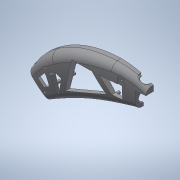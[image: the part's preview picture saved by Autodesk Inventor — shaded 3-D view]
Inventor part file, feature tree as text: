
AUTODESK INVENTOR PART (.ipt)
format: ipt  version: 2020 (Build 240168000, 168)  size: 6,243,840 bytes
history: native  units: in
note: dims shown in document units (in); Inventor stores cm internally (conversion verified against a paired STEP export)
features: extrude x17, sketch x9, other x5, fillet x4, projected_geometry x4, surface_op x2, revolve x2, boolean_combine x1, split x1, chamfer x1, plane x1, delete_face x1, mirror x1, imported_body x1
ambient origin geometry x8: Origin, YZ Plane, XZ Plane, XY Plane, X Axis, Y Axis, Z Axis, Center Point
bodies: Solid1 (feature_tree), Solid196 (feature_tree), Solid197 (feature_tree)
feature tree (50):
  other  "Repaired Geometry1"
  surface_op  "Stitch Surface1"
  sketch  "Sketch2-<F>"  dims[d0=0.03in d1=0.198in]
  extrude  "Extrusion1"  Depth=0.198in
  extrude  "Extrusion2"  Depth=0.184in
  surface_op  "Stitch Surface2"
  boolean_combine  "Combine2"
  split  "Split1"
  extrude  "Extrusion4"  Depth=0.268in
  sketch  "Sketch5-<F>"  dims[d2=0.21in d3=0.184in]
  extrude  "Extrusion5"  Depth=0.4in
  extrude  "Extrusion6"  Depth=0.158in TaperAngle=0.0deg
  extrude  "Extrusion7"  Depth=0.03in
  sketch  "Sketch7-<F>"  dims[d4=0.158in d5=0.0in d7=0.268in]
  extrude  "Extrusion8"  Depth=0.329in
  revolve  "Revolution1"  [1 undecoded]
  revolve  "Revolution2"  [1 undecoded]
  fillet  "Fillet1"  Radius=1.086in
  extrude  "Extrusion9"  Depth=0.423in
  sketch  "Sketch8-<F>"  dims[d8=1.512in d9=0.4in]
  extrude  "Extrusion10"  Depth=0.88in
  extrude  "Extrusion11"  Depth=1.0in
  extrude  "Extrusion12"  Depth=1.03in
  extrude  "Extrusion13"  Depth=1.053in
  chamfer  "Chamfer1"  Distance=1.125in
  extrude  "Extrusion14"  Depth=0.044in
  plane  "Work Plane2"
  extrude  "Extrusion15"  Depth=0.09in
  extrude  "Extrusion16"  Depth=0.17in
  delete_face  "Delete Face2"
  extrude  "Extrusion17"  Depth=0.24in
  fillet  "Fillet3"  Radius=0.244in
  fillet  "Fillet4"  Radius=0.025in
  fillet  "Fillet5"  Radius=0.016in
  mirror  "Mirror1"
  extrude  "Extrusion18"  Depth=0.097in
  other  "Srf3"
  other  "Srf4"
  imported_body  "Base1"
  sketch  "Sketch6-<F>"  dims[d10=0.7in d11=0.158in d12=0.0in]
  sketch  "Sketch9-<F>"  dims[d16=0.004in d17=0.004in d18=0.03in]
  sketch  "Sketch10-<F>"  dims[d19=0.07in]
  projected_geometry  "Projected Loop1"
  sketch  "Sketch11-<F>"  dims[d20=0.031in d45=0.121in d46=0.03in d47=0.158in d48=0.03in d49=0.03in d50=0.03in d51=0.03in d52=0.03in d53=0.03in d54=0.03in d55=0.06in d56=0.03in d57=0.03in d59=0.0962in d60=0.329in]
  sketch  "Sketch12-<F>"  dims[d61=0.595in d62=0.85in d63=0.975in d64=1.086in d66=0.423in d67=0.88in d68=1.0in d69=1.03in d70=1.053in d71=1.125in d72=0.044in d73=0.09in d74=0.17in d75=0.24in d76=0.244in d77=0.025in d78=0.016in d79=0.097in d80=0.23in d83=0.225in d84=0.4in d85=0.4055in d86=0.4785in d87=0.4in d88=0.05in d89=1.2in d90=0.0625in d91=0.0in d92=0.2205in d93=0.0206in d94=0.0495in d95=0.0in d96=0.0755in d97=0.0in d124=0.043in d131=0.055in d132=0.11in d133=0.055in d134=0.0235in d135=0.086in d136=0.043in d139=0.045in d141=0.043in d147=0.0235in d148=0.11in d149=0.055in d150=0.2508in d151=0.075in d153=0.0035in d154=0.0035in d155=0.043in d156=0.045in d157=0.055in d158=0.0in d159=90.0deg d160=90.0deg d161=0.04in d162=0.091in d163=0.034in d164=0.064in d165=0.3105in d166=0.025in d167=0.025in d168=0.025in d169=0.025in d170=1.065in d171=1.0in d172=0.0in d173=0.126in d174=0.101in d175=0.108in d176=0.02in d177=0.0in d178=0.009in d179=0.009in d181=1.5748in d183=360.0deg d185=0.012in d186=0.0in d187=0.02in d188=0.0in d189=1.0in d190=0.0in d191=0.02in d192=0.125in d193=0.1374in d194=0.1271in d195=0.159in d196=0.05in d197=0.237in d198=0.317in d199=0.023in d200=1.115in d201=0.2205in d202=0.0in d203=0.07in d204=0.3in d205=-0.1175in d206=0.023in d207=0.0in d208=0.015in d209=0.0in d211=0.03in d212=0.15in d213=0.061in d214=0.0in d216=0.059in d217=0.015in d218=0.004in d219=0.015in d220=0.03in d221=0.059in d222=0.15in d223=0.015in d224=0.275in d225=0.4989in d226=0.014in d227=0.1099in d228=0.015in d229=0.0618in d230=0.014in d231=0.0262in d232=0.0in d233=0.01in]
  projected_geometry  "Projected Loop2"
  projected_geometry  "Projected Loop3"
  projected_geometry  "Projected Loop4"
  other  "OffsetSrf2"
  other  "OffsetSrf1"
note: 2 required parameter values undecoded (feature->parameter linkage not recoverable at this tier; creation-order binding heuristic only, values carry confidence <= 0.55)
